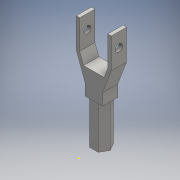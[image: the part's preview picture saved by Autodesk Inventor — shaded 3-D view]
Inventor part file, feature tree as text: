
AUTODESK INVENTOR PART (.ipt)
format: ipt  version: 2016 (Build 200138000, 138)  size: 147,456 bytes
history: native  units: mm
features: sketch x5, extrude x4
ambient origin geometry x8: Origin, YZ Plane, XZ Plane, XY Plane, X Axis, Y Axis, Z Axis, Center Point
bodies: Solid1 (feature_tree)
feature tree (9):
  extrude  "Extrusion1"  Depth=18.0mm TaperAngle=0.0deg
  extrude  "Extrusion2"  Depth=1.5mm
  sketch  "Sketch3"  dims[d16=27.824719mm d17=11.0mm]
  extrude  "Extrusion3"  Depth=11.0mm
  extrude  "Extrusion4"  Depth=6.5mm TaperAngle=0.0deg
  sketch  "Sketch1"  dims[d0=7.5mm d1=18.0mm d2=0.0mm]
  sketch  "Sketch2"  dims[d12=1.5mm d13=1.5mm]
  sketch  "Sketch5"  dims[d21=12.0mm d22=6.5mm d23=0.0mm]
  sketch  "Sketch6"  dims[d25=6.5mm d26=0.0mm d27=6.0mm d28=3.0mm d29=6.5mm d30=0.0mm]
